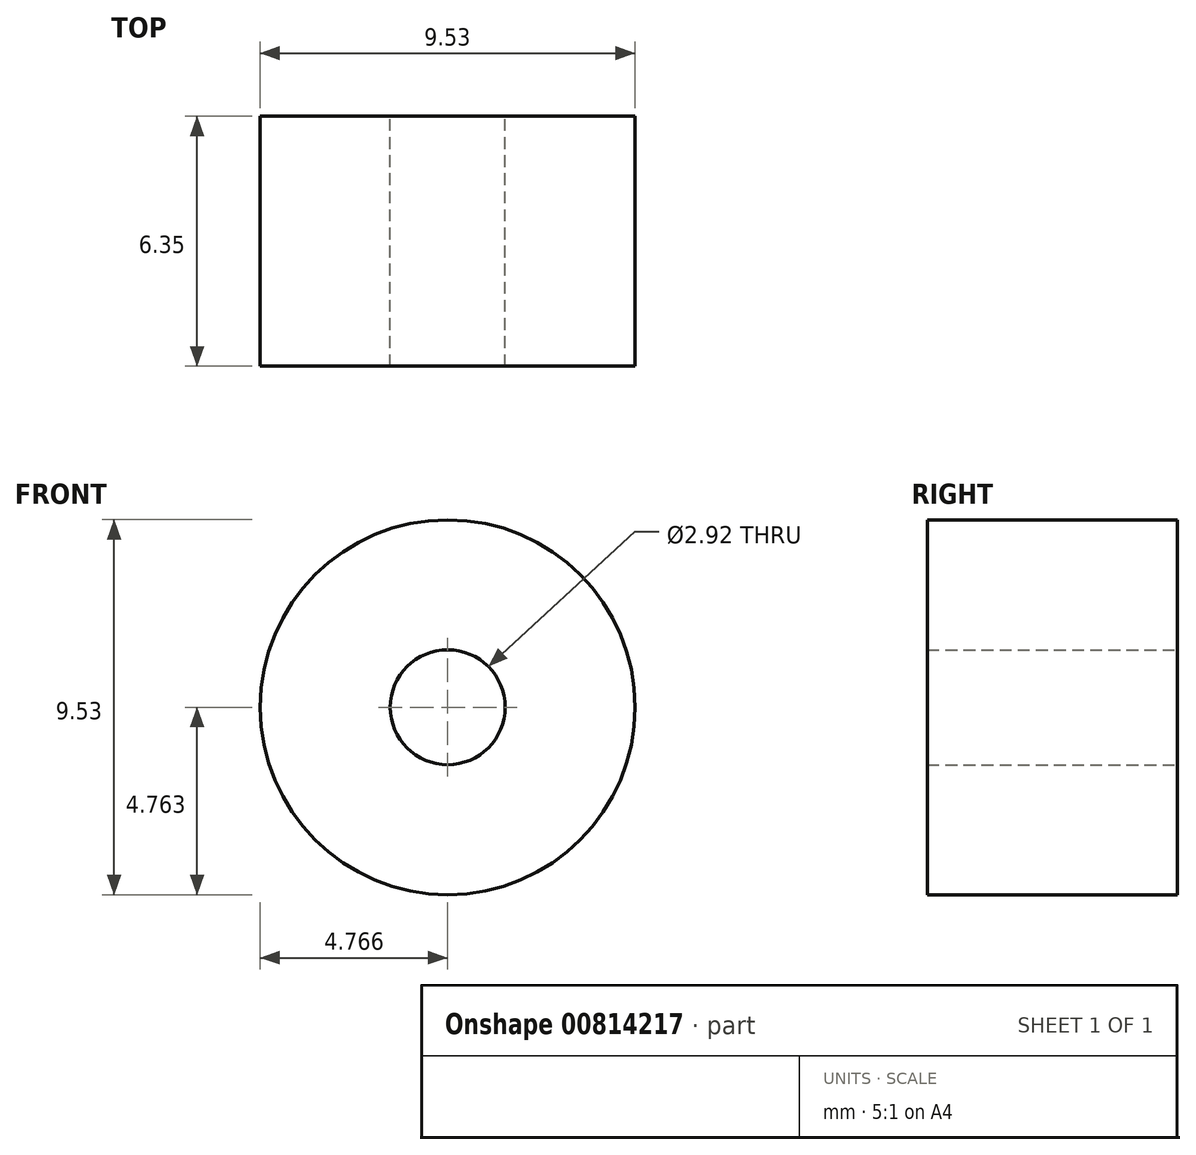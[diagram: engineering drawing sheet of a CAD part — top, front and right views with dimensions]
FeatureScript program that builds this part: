
annotation { "Feature Type Name" : "Feature", "Feature Type Description" : "" }
export const myFeature = defineFeature(function(context is Context, id is Id, definition is map)
    precondition{}
    {
        {
            var Q0;
            Q0=qCreatedBy(makeId("Front.planeOp"),FACE);
            var sketch = newSketch(context, id + "F0", { "sketchPlane" : qUnion([Q0])});
            skCircle(sketch, "E0", {"center": v(-52.8, 53.84) * mm, "radius": 4.76 * mm});
            skCircle(sketch, "E1", {"center": v(-52.8, 53.84) * mm, "radius": 1.46 * mm});
            skSolve(sketch);
        }
        {
            var Q0;
            Q0=makeQuery(id+"F0.imprint","IMPRINT",FACE,{"disambiguationData":[TD([[makeQuery(id+"F0.imprint","IMPRINT",EDGE,{"derivedFrom":sQuery(id+"F0.wireOp",EDGE,"E0")}),1.0]])]});
            extrude(context, id + "F1", {"entities" : qUnion([Q0]), "depth" : 6.35 * mm, "offsetDistance" : 25.4 * mm});
        }
    });
